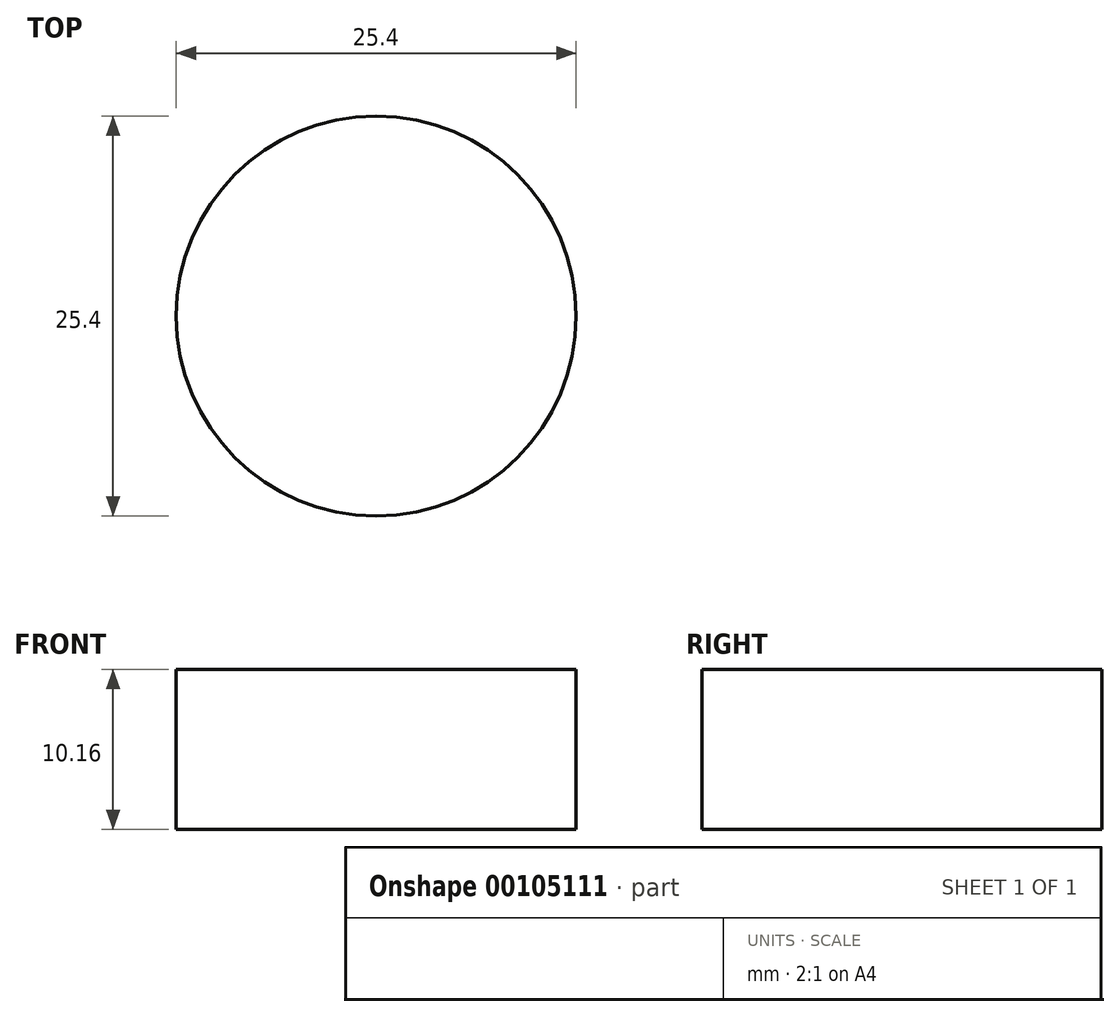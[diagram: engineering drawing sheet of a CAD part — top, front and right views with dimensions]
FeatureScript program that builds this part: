
annotation { "Feature Type Name" : "Feature", "Feature Type Description" : "" }
export const myFeature = defineFeature(function(context is Context, id is Id, definition is map)
    precondition{}
    {
        {
            var Q0;
            Q0=qCreatedBy(makeId("Top.planeOp"),FACE);
            var sketch = newSketch(context, id + "F0", { "sketchPlane" : qUnion([Q0])});
            skCircle(sketch, "E0", {"center": v(0, 0) * mm, "radius": 12.7 * mm});
            skSolve(sketch);
        }
        {
            var Q0;
            Q0 = qSketchRegion(id + "F0", true);
            extrude(context, id + "F1", {"entities" : qUnion([Q0]), "depth" : 10.16 * mm});
        }
    });
